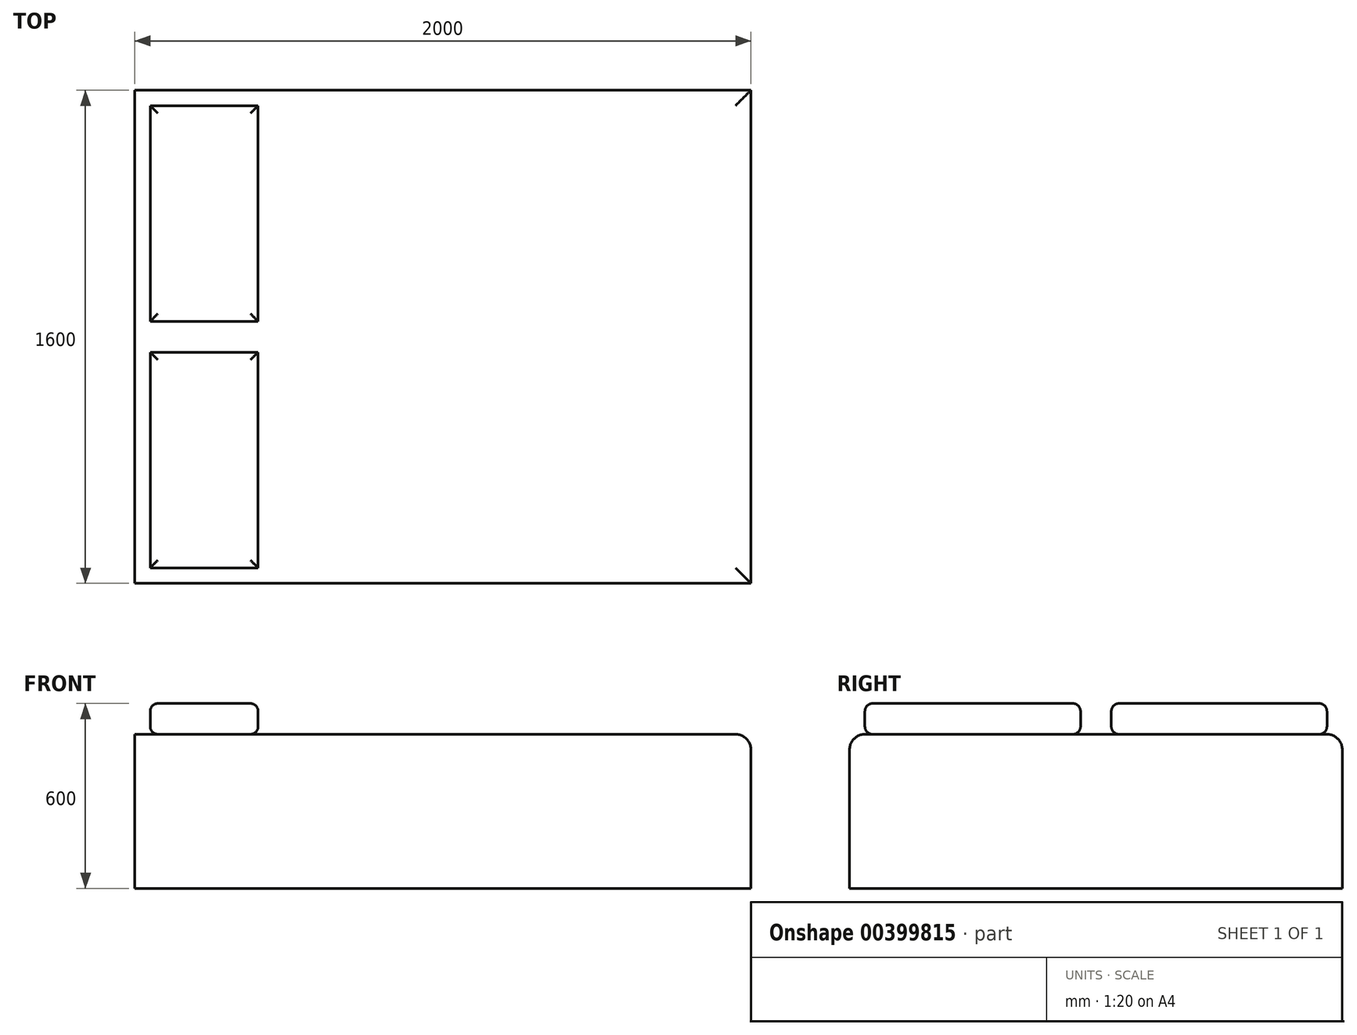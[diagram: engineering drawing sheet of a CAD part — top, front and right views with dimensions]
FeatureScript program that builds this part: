
annotation { "Feature Type Name" : "Feature", "Feature Type Description" : "" }
export const myFeature = defineFeature(function(context is Context, id is Id, definition is map)
    precondition{}
    {
        {
            var Q0;
            Q0=qCreatedBy(makeId("Top.planeOp"),FACE);
            var sketch = newSketch(context, id + "F0", { "sketchPlane" : qUnion([Q0])});
            skLineSegment(sketch, "E0.bottom", {"start": v(0, 0) * mm, "end": v(2000, 0) * mm});
            skLineSegment(sketch, "E0.top", {"start": v(0, 1600) * mm, "end": v(2000, 1600) * mm});
            skLineSegment(sketch, "E0.left", {"start": v(0, 0) * mm, "end": v(0, 1600) * mm});
            skLineSegment(sketch, "E0.right", {"start": v(2000, 0) * mm, "end": v(2000, 1600) * mm});
            skSolve(sketch);
        }
        {
            var Q0;
            Q0 = qSketchRegion(id + "F0", true);
            extrude(context, id + "F1", {"entities" : qUnion([Q0]), "depth" : 500 * mm});
        }
        {
            var Q0;
            Q0=makeQuery(id+"F1.opExtrude","CAP_FACE",FACE,{"disambiguationData":[OSD([sQuery(id+"F0.wireOp",EDGE,"E0.bottom"),sQuery(id+"F0.wireOp",EDGE,"E0.top"),sQuery(id+"F0.wireOp",EDGE,"E0.left"),sQuery(id+"F0.wireOp",EDGE,"E0.right")])],"isStart":false});
            var sketch = newSketch(context, id + "F2", { "sketchPlane" : qUnion([Q0])});
            skLineSegment(sketch, "E1.bottom", {"start": v(50, 50) * mm, "end": v(400, 50) * mm});
            skLineSegment(sketch, "E1.top", {"start": v(50, 750) * mm, "end": v(400, 750) * mm});
            skLineSegment(sketch, "E1.left", {"start": v(50, 50) * mm, "end": v(50, 750) * mm});
            skLineSegment(sketch, "E1.right", {"start": v(400, 50) * mm, "end": v(400, 750) * mm});
            skLineSegment(sketch, "E2.bottom", {"start": v(50, 1550) * mm, "end": v(400, 1550) * mm});
            skLineSegment(sketch, "E2.top", {"start": v(50, 850) * mm, "end": v(400, 850) * mm});
            skLineSegment(sketch, "E2.left", {"start": v(50, 1550) * mm, "end": v(50, 850) * mm});
            skLineSegment(sketch, "E2.right", {"start": v(400, 1550) * mm, "end": v(400, 850) * mm});
            skSolve(sketch);
        }
        {
            var Q0;
            Q0 = qSketchRegion(id + "F2", true);
            extrude(context, id + "F3", {"entities" : qUnion([Q0]), "depth" : 100 * mm});
        }
        {
            var Q0;
            Q0=makeQuery(id+"F3.opExtrude","CAP_EDGE",EDGE,{"disambiguationData":[OSD([sQuery(id+"F2.wireOp",EDGE,"E1.bottom")])],"isStart":false});
            var Q1;
            Q1=makeQuery(id+"F3.opExtrude","CAP_EDGE",EDGE,{"disambiguationData":[OSD([sQuery(id+"F2.wireOp",EDGE,"E1.left")])],"isStart":false});
            var Q2;
            Q2=makeQuery(id+"F3.opExtrude","CAP_EDGE",EDGE,{"disambiguationData":[OSD([sQuery(id+"F2.wireOp",EDGE,"E1.top")])],"isStart":false});
            var Q3;
            Q3=makeQuery(id+"F3.opExtrude","CAP_EDGE",EDGE,{"disambiguationData":[OSD([sQuery(id+"F2.wireOp",EDGE,"E1.right")])],"isStart":false});
            var Q4;
            Q4=makeQuery(id+"F3.opExtrude","CAP_EDGE",EDGE,{"disambiguationData":[OSD([sQuery(id+"F2.wireOp",EDGE,"E1.bottom")])],"isStart":true});
            var Q5;
            Q5=makeQuery(id+"F3.opExtrude","CAP_EDGE",EDGE,{"disambiguationData":[OSD([sQuery(id+"F2.wireOp",EDGE,"E1.right")])],"isStart":true});
            var Q6;
            Q6=makeQuery(id+"F3.opExtrude","CAP_EDGE",EDGE,{"disambiguationData":[OSD([sQuery(id+"F2.wireOp",EDGE,"E1.left")])],"isStart":true});
            var Q7;
            Q7=makeQuery(id+"F3.opExtrude","CAP_EDGE",EDGE,{"disambiguationData":[OSD([sQuery(id+"F2.wireOp",EDGE,"E1.top")])],"isStart":true});
            var Q8;
            Q8=makeQuery(id+"F3.opExtrude","CAP_EDGE",EDGE,{"disambiguationData":[OSD([sQuery(id+"F2.wireOp",EDGE,"E2.left")])],"isStart":false});
            var Q9;
            Q9=makeQuery(id+"F3.opExtrude","CAP_EDGE",EDGE,{"disambiguationData":[OSD([sQuery(id+"F2.wireOp",EDGE,"E2.top")])],"isStart":false});
            var Q10;
            Q10=makeQuery(id+"F3.opExtrude","CAP_EDGE",EDGE,{"disambiguationData":[OSD([sQuery(id+"F2.wireOp",EDGE,"E2.right")])],"isStart":false});
            var Q11;
            Q11=makeQuery(id+"F3.opExtrude","CAP_EDGE",EDGE,{"disambiguationData":[OSD([sQuery(id+"F2.wireOp",EDGE,"E2.bottom")])],"isStart":false});
            var Q12;
            Q12=makeQuery(id+"F3.opExtrude","CAP_EDGE",EDGE,{"disambiguationData":[OSD([sQuery(id+"F2.wireOp",EDGE,"E2.left")])],"isStart":true});
            var Q13;
            Q13=makeQuery(id+"F3.opExtrude","CAP_EDGE",EDGE,{"disambiguationData":[OSD([sQuery(id+"F2.wireOp",EDGE,"E2.top")])],"isStart":true});
            var Q14;
            Q14=makeQuery(id+"F3.opExtrude","CAP_EDGE",EDGE,{"disambiguationData":[OSD([sQuery(id+"F2.wireOp",EDGE,"E2.bottom")])],"isStart":true});
            var Q15;
            Q15=makeQuery(id+"F3.opExtrude","CAP_EDGE",EDGE,{"disambiguationData":[OSD([sQuery(id+"F2.wireOp",EDGE,"E2.right")])],"isStart":true});
            fillet(context, id + "F4", {"entities" : qUnion([Q0, Q1, Q2, Q3, Q4, Q5, Q6, Q7, Q8, Q9, Q10, Q11, Q12, Q13, Q14, Q15]), "radius" : 25 * mm, "tangentPropagation" : true, "allowEdgeOverflow" : false});
        }
        {
            var Q0;
            Q0=makeQuery(id+"F1.opExtrude","CAP_EDGE",EDGE,{"disambiguationData":[OSD([sQuery(id+"F0.wireOp",EDGE,"E0.bottom")])],"isStart":false});
            var Q1;
            Q1=makeQuery(id+"F1.opExtrude","CAP_EDGE",EDGE,{"disambiguationData":[OSD([sQuery(id+"F0.wireOp",EDGE,"E0.right")])],"isStart":false});
            var Q2;
            Q2=makeQuery(id+"F1.opExtrude","CAP_EDGE",EDGE,{"disambiguationData":[OSD([sQuery(id+"F0.wireOp",EDGE,"E0.top")])],"isStart":false});
            fillet(context, id + "F5", {"entities" : qUnion([Q0, Q1, Q2]), "radius" : 50 * mm, "tangentPropagation" : true, "allowEdgeOverflow" : false});
        }
    });
